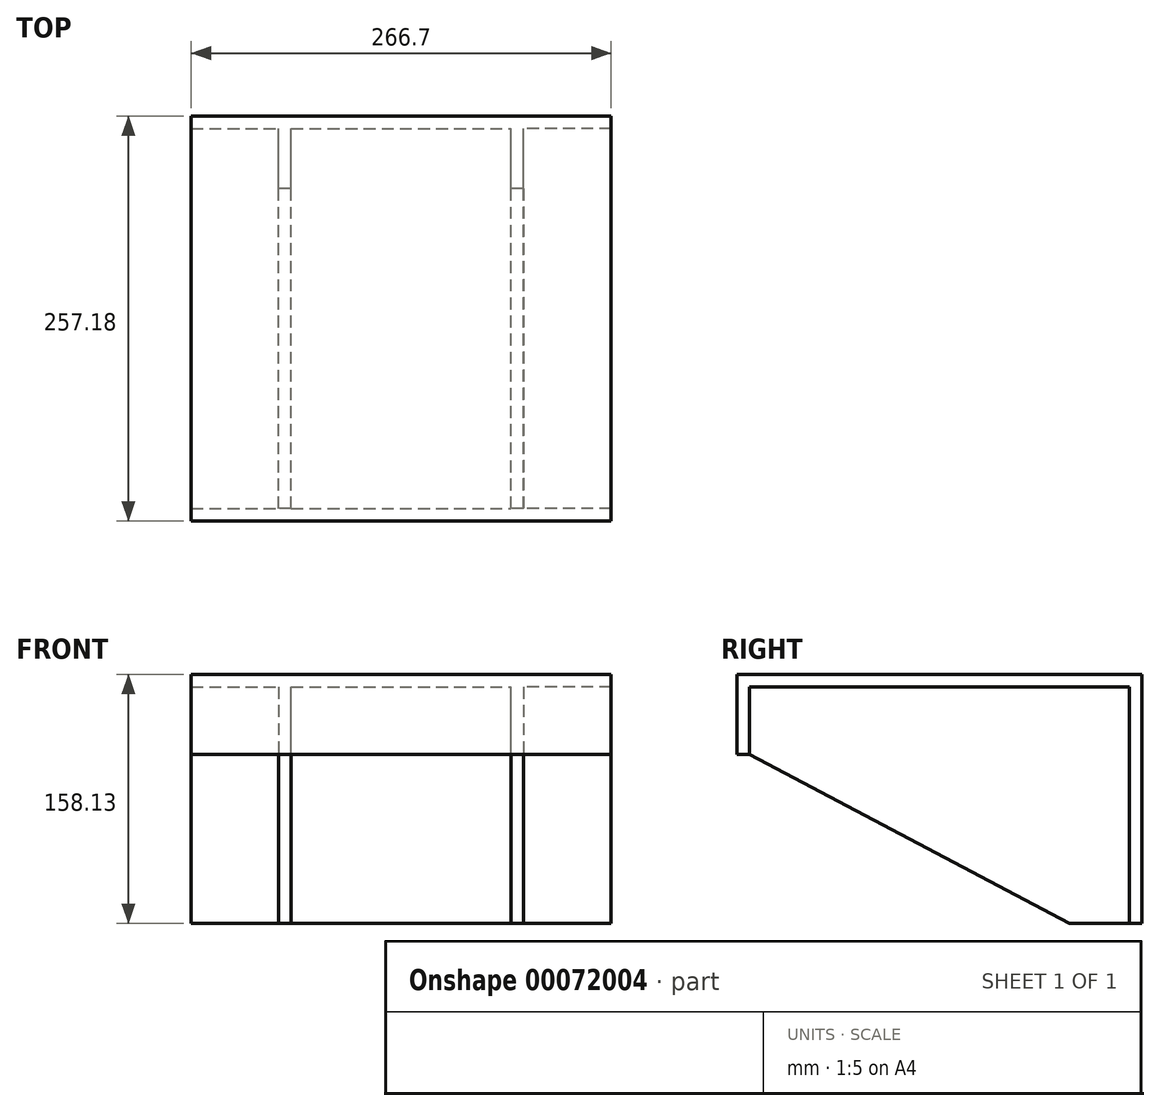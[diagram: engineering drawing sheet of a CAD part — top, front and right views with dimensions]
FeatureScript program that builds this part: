
annotation { "Feature Type Name" : "Feature", "Feature Type Description" : "" }
export const myFeature = defineFeature(function(context is Context, id is Id, definition is map)
    precondition{}
    {
        {
            var Q0;
            Q0=qCreatedBy(makeId("Front.planeOp"),FACE);
            var sketch = newSketch(context, id + "F0", { "sketchPlane" : qUnion([Q0])});
            skLineSegment(sketch, "E0.bottom", {"start": v(-133.35, 0) * mm, "end": v(133.35, 0) * mm});
            skLineSegment(sketch, "E0.top", {"start": v(-133.35, -158.13) * mm, "end": v(133.35, -158.13) * mm});
            skLineSegment(sketch, "E0.left", {"start": v(-133.35, 0) * mm, "end": v(-133.35, -158.13) * mm});
            skLineSegment(sketch, "E0.right", {"start": v(133.35, 0) * mm, "end": v(133.35, -158.13) * mm});
            skSolve(sketch);
        }
        {
            var Q0;
            Q0=makeQuery(id+"F0.imprint","IMPRINT",FACE,{"disambiguationData":[TD([[makeQuery(id+"F0.imprint","IMPRINT",EDGE,{"derivedFrom":sQuery(id+"F0.wireOp",EDGE,"E0.bottom")}),-1.0]])]});
            extrude(context, id + "F1", {"entities" : qUnion([Q0]), "depth" : 7.94 * mm});
        }
        {
            var Q0;
            Q0=makeQuery(id+"F1.opExtrude","CAP_FACE",FACE,{"disambiguationData":[OSD([sQuery(id+"F0.wireOp",EDGE,"E0.bottom"),sQuery(id+"F0.wireOp",EDGE,"E0.top"),sQuery(id+"F0.wireOp",EDGE,"E0.left"),sQuery(id+"F0.wireOp",EDGE,"E0.right")])],"isStart":false});
            var sketch = newSketch(context, id + "F2", { "sketchPlane" : qUnion([Q0])});
            skLineSegment(sketch, "E1.bottom", {"start": v(-112.71, -75.58) * mm, "end": v(112.71, -75.58) * mm});
            skLineSegment(sketch, "E1.top", {"start": v(-112.71, -139.08) * mm, "end": v(112.71, -139.08) * mm});
            skLineSegment(sketch, "E1.left", {"start": v(-112.71, -75.58) * mm, "end": v(-112.71, -139.08) * mm});
            skLineSegment(sketch, "E1.right", {"start": v(112.71, -75.58) * mm, "end": v(112.71, -139.08) * mm});
            skSolve(sketch);
        }
        {
            var Q0;
            Q0=makeQuery(id+"F1.opExtrude","CAP_FACE",FACE,{"disambiguationData":[OSD([sQuery(id+"F0.wireOp",EDGE,"E0.bottom"),sQuery(id+"F0.wireOp",EDGE,"E0.top"),sQuery(id+"F0.wireOp",EDGE,"E0.left"),sQuery(id+"F0.wireOp",EDGE,"E0.right")])],"isStart":false});
            var sketch = newSketch(context, id + "F3", { "sketchPlane" : qUnion([Q0])});
            skLineSegment(sketch, "E2", {"start": v(-133.35, 0) * mm, "end": v(-133.35, -7.94) * mm});
            skLineSegment(sketch, "E3", {"start": v(-133.35, -7.94) * mm, "end": v(-77.79, -7.94) * mm});
            skLineSegment(sketch, "E4", {"start": v(-77.79, -7.94) * mm, "end": v(-77.79, -158.13) * mm});
            skLineSegment(sketch, "E5", {"start": v(-77.79, -158.13) * mm, "end": v(-69.85, -158.13) * mm});
            skLineSegment(sketch, "E6", {"start": v(-69.85, -158.13) * mm, "end": v(-69.85, -7.94) * mm});
            skLineSegment(sketch, "E7.MirrorCS", {"start": v(133.35, -7.94) * mm, "end": v(77.79, -7.94) * mm});
            skLineSegment(sketch, "E8.MirrorCS", {"start": v(69.85, -158.13) * mm, "end": v(69.85, -7.94) * mm});
            skLineSegment(sketch, "E9.MirrorCS", {"start": v(77.79, -7.94) * mm, "end": v(77.79, -158.13) * mm});
            skLineSegment(sketch, "E10.MirrorCS", {"start": v(77.79, -158.13) * mm, "end": v(69.85, -158.13) * mm});
            skLineSegment(sketch, "E11.MirrorCS", {"start": v(133.35, 0) * mm, "end": v(133.35, -7.94) * mm});
            skLineSegment(sketch, "E12", {"start": v(-69.85, -7.94) * mm, "end": v(69.85, -7.94) * mm});
            skLineSegment(sketch, "E13", {"start": v(-133.35, 0) * mm, "end": v(133.35, 0) * mm});
            skSolve(sketch);
        }
        {
            var Q0;
            Q0=qSketchRegion(id+"F3",true);
            extrude(context, id + "F4", {"entities" : qUnion([Q0]), "operationType" : NewBodyOperationType.ADD, "depth" : 241.3 * mm});
        }
        {
            var Q0;
            Q0=makeQuery(id+"F4.opExtrude","SWEPT_FACE",FACE,{"disambiguationData":[OSD([sQuery(id+"F3.wireOp",EDGE,"E4")])]});
            var sketch = newSketch(context, id + "F5", { "sketchPlane" : qUnion([Q0])});
            skLineSegment(sketch, "E14", {"start": v(46.04, -158.13) * mm, "end": v(249.24, -158.13) * mm});
            skLineSegment(sketch, "E15", {"start": v(249.24, -158.13) * mm, "end": v(249.24, -50.8) * mm});
            skLineSegment(sketch, "E16", {"start": v(249.24, -50.8) * mm, "end": v(46.04, -158.13) * mm});
            skSolve(sketch);
        }
        {
            var Q0;
            Q0=qSketchRegion(id+"F5",true);
            extrude(context, id + "F6", {"entities" : qUnion([Q0]), "operationType" : NewBodyOperationType.REMOVE, "endBound" : BoundingType.THROUGH_ALL, "oppositeDirection" : true, "depth" : 25.4 * mm});
        }
        {
            var Q0;
            Q0=makeQuery(id+"F4.boolean.opBoolean","MERGE",FACE,{"derivedFrom":[makeQuery(id+"F1.opExtrude","SWEPT_FACE",FACE,{"disambiguationData":[OSD([sQuery(id+"F0.wireOp",EDGE,"E0.bottom")])]}),makeQuery(id+"F4.opExtrude","SWEPT_FACE",FACE,{"disambiguationData":[OSD([sQuery(id+"F3.wireOp",EDGE,"E13")])]})]});
            var sketch = newSketch(context, id + "F7", { "sketchPlane" : qUnion([Q0])});
            skLineSegment(sketch, "E17.bottom", {"start": v(-48.99, -120.8) * mm, "end": v(51.01, -120.8) * mm});
            skLineSegment(sketch, "E17.top", {"start": v(-48.99, -220.8) * mm, "end": v(51.01, -220.8) * mm});
            skLineSegment(sketch, "E17.left", {"start": v(-48.99, -120.8) * mm, "end": v(-48.99, -220.8) * mm});
            skLineSegment(sketch, "E17.right", {"start": v(51.01, -120.8) * mm, "end": v(51.01, -220.8) * mm});
            skSolve(sketch);
        }
        {
            var Q0;
            Q0=makeQuery(id+"F4.opExtrude","CAP_FACE",FACE,{"disambiguationData":[OSD([sQuery(id+"F3.wireOp",EDGE,"E2"),sQuery(id+"F3.wireOp",EDGE,"E3"),sQuery(id+"F3.wireOp",EDGE,"E4"),sQuery(id+"F3.wireOp",EDGE,"E5"),sQuery(id+"F3.wireOp",EDGE,"E6"),sQuery(id+"F3.wireOp",EDGE,"E7.MirrorCS"),sQuery(id+"F3.wireOp",EDGE,"E8.MirrorCS"),sQuery(id+"F3.wireOp",EDGE,"E9.MirrorCS"),sQuery(id+"F3.wireOp",EDGE,"E10.MirrorCS"),sQuery(id+"F3.wireOp",EDGE,"E11.MirrorCS"),sQuery(id+"F3.wireOp",EDGE,"E12"),sQuery(id+"F3.wireOp",EDGE,"E13")])],"isStart":false});
            var sketch = newSketch(context, id + "F8", { "sketchPlane" : qUnion([Q0])});
            skLineSegment(sketch, "E18.bottom", {"start": v(-133.35, 0) * mm, "end": v(133.35, 0) * mm});
            skLineSegment(sketch, "E18.top", {"start": v(-133.35, -50.8) * mm, "end": v(133.35, -50.8) * mm});
            skLineSegment(sketch, "E18.left", {"start": v(-133.35, 0) * mm, "end": v(-133.35, -50.8) * mm});
            skLineSegment(sketch, "E18.right", {"start": v(133.35, 0) * mm, "end": v(133.35, -50.8) * mm});
            skSolve(sketch);
        }
        {
            var Q0;
            Q0=qSketchRegion(id+"F8",true);
            extrude(context, id + "F9", {"entities" : qUnion([Q0]), "operationType" : NewBodyOperationType.ADD, "depth" : 7.94 * mm});
        }
    });
